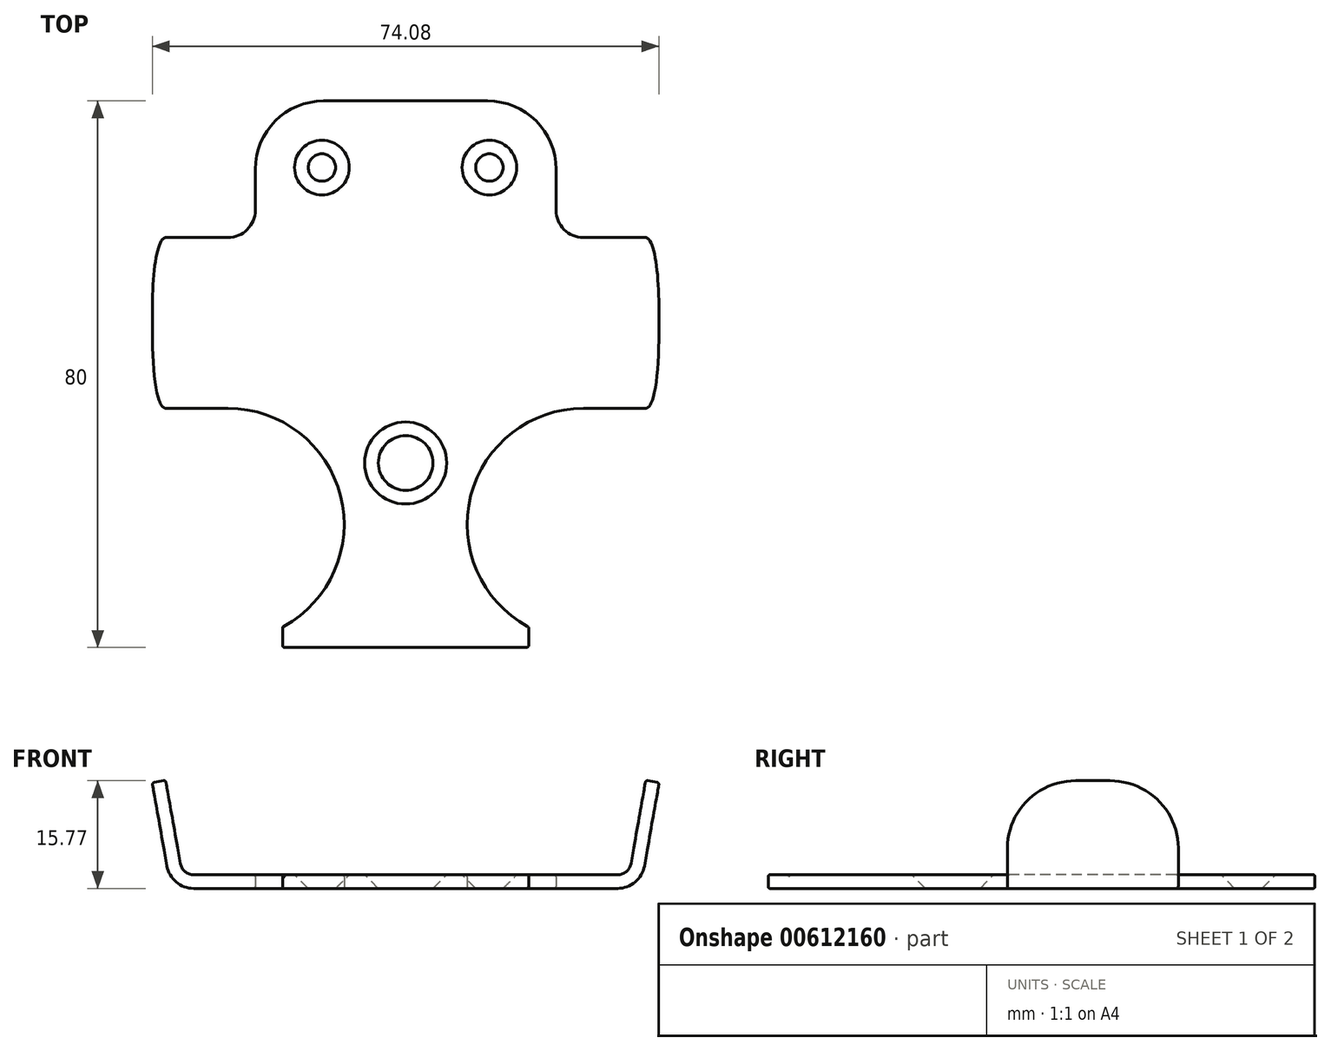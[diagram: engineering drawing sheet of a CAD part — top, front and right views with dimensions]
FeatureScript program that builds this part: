
annotation { "Feature Type Name" : "Feature", "Feature Type Description" : "" }
export const myFeature = defineFeature(function(context is Context, id is Id, definition is map)
    precondition{}
    {
        {
            var Q0;
            Q0=qCreatedBy(makeId("Top.planeOp"),FACE);
            var sketch = newSketch(context, id + "F0", { "sketchPlane" : qUnion([Q0])});
            skLineSegment(sketch, "E0", {"start": v(0, -42) * mm, "end": v(0, 38) * mm, "construction": true});
            skLineSegment(sketch, "E1", {"start": v(0, 38) * mm, "end": v(-12, 38) * mm});
            skArc(sketch, "E2", {"start": v(-12, 38) * mm, "mid": v(-19.07, 35.07) * mm, "end": v(-22, 28) * mm});
            skLineSegment(sketch, "E3", {"start": v(-22, 28) * mm, "end": v(-22, 22) * mm});
            skArc(sketch, "E4", {"start": v(-22, 22) * mm, "mid": v(-23.17, 19.17) * mm, "end": v(-26, 18) * mm});
            skLineSegment(sketch, "E5", {"start": v(-26, 18) * mm, "end": v(-28.5, 18) * mm});
            skLineSegment(sketch, "E6", {"start": v(-28.5, 18) * mm, "end": v(-28.5, -7) * mm});
            skLineSegment(sketch, "E7", {"start": v(-28.5, -7) * mm, "end": v(-26, -7) * mm});
            skArc(sketch, "E8", {"start": v(-18, -39) * mm, "mid": v(-9.5, -19.88) * mm, "end": v(-26, -7) * mm});
            skLineSegment(sketch, "E9", {"start": v(-18, -39) * mm, "end": v(-18, -42) * mm});
            skLineSegment(sketch, "E10", {"start": v(-18, -42) * mm, "end": v(0, -42) * mm});
            skLineSegment(sketch, "E11.MirrorCS", {"start": v(0, 38) * mm, "end": v(12, 38) * mm});
            skArc(sketch, "E12.MirrorCS", {"start": v(12, 38) * mm, "mid": v(19.07, 35.07) * mm, "end": v(22, 28) * mm});
            skLineSegment(sketch, "E13.MirrorCS", {"start": v(22, 28) * mm, "end": v(22, 22) * mm});
            skArc(sketch, "E14.MirrorCS", {"start": v(22, 22) * mm, "mid": v(23.17, 19.17) * mm, "end": v(26, 18) * mm});
            skLineSegment(sketch, "E15.MirrorCS", {"start": v(26, 18) * mm, "end": v(28.5, 18) * mm});
            skLineSegment(sketch, "E16.MirrorCS", {"start": v(28.5, 18) * mm, "end": v(28.5, -7) * mm});
            skLineSegment(sketch, "E17.MirrorCS", {"start": v(28.5, -7) * mm, "end": v(26, -7) * mm});
            skArc(sketch, "E18.MirrorCS", {"start": v(18, -39) * mm, "mid": v(9.5, -19.88) * mm, "end": v(26, -7) * mm});
            skLineSegment(sketch, "E19.MirrorCS", {"start": v(18, -39) * mm, "end": v(18, -42) * mm});
            skLineSegment(sketch, "E20.MirrorCS", {"start": v(18, -42) * mm, "end": v(0, -42) * mm});
            skSolve(sketch);
        }
        {
            var Q0;
            Q0 = qSketchRegion(id + "F0", true);
            extrude(context, id + "F1", {"entities" : qUnion([Q0]), "depth" : 2 * mm, "offsetDistance" : 25 * mm});
        }
        {
            var Q0;
            Q0=makeQuery(id+"F1.opExtrude","SWEPT_FACE",FACE,{"disambiguationData":[OSD([sQuery(id+"F0.wireOp",EDGE,"E7")])]});
            var sketch = newSketch(context, id + "F2", { "sketchPlane" : qUnion([Q0])});
            skLineSegment(sketch, "E21", {"start": v(-28.5, 0) * mm, "end": v(-31, 0) * mm});
            skArc(sketch, "E22", {"start": v(-34.94, 3.3) * mm, "mid": v(-33.57, 0.94) * mm, "end": v(-31, 0) * mm});
            skLineSegment(sketch, "E23", {"start": v(-34.94, 3.3) * mm, "end": v(-35.35, 5.62) * mm});
            skLineSegment(sketch, "E24", {"start": v(-35.35, 5.62) * mm, "end": v(-33.38, 5.97) * mm});
            skLineSegment(sketch, "E25", {"start": v(-33.38, 5.97) * mm, "end": v(-32.97, 3.65) * mm});
            skArc(sketch, "E26", {"start": v(-32.97, 3.65) * mm, "mid": v(-32.29, 2.47) * mm, "end": v(-31, 2) * mm});
            skLineSegment(sketch, "E27", {"start": v(-31, 2) * mm, "end": v(-28.5, 2) * mm});
            skSolve(sketch);
        }
        {
            var Q0;
            Q0 = qSketchRegion(id + "F2", true);
            var Q1;
            Q1=makeQuery(id+"F2.imprint","IMPRINT",FACE,{"disambiguationData":[TD([[makeQuery(id+"F2.imprint","IMPRINT",EDGE,{"derivedFrom":sQuery(id+"F2.wireOp",EDGE,"E21")}),-1.0]])]});
            var Q2;
            Q2=makeQuery(id+"F1.opExtrude","SWEPT_FACE",FACE,{"disambiguationData":[OSD([sQuery(id+"F0.wireOp",EDGE,"E5")])]});
            extrude(context, id + "F3", {"entities" : qUnion([Q0, Q1]), "endBound" : BoundingType.UP_TO_SURFACE, "oppositeDirection" : true, "depth" : 25 * mm, "endBoundEntityFace" : qUnion([Q2]), "offsetDistance" : 25 * mm});
        }
        {
            var Q0;
            Q0=makeQuery(id+"F3.opExtrude","SWEPT_FACE",FACE,{"disambiguationData":[OSD([sQuery(id+"F2.wireOp",EDGE,"E23")])]});
            var sketch = newSketch(context, id + "F4", { "sketchPlane" : qUnion([Q0])});
            skArc(sketch, "E28", {"start": v(-8, 21.67) * mm, "mid": v(-15.07, 18.75) * mm, "end": v(-18, 11.67) * mm});
            skArc(sketch, "E29", {"start": v(7, 11.67) * mm, "mid": v(4.07, 18.75) * mm, "end": v(-3, 21.67) * mm});
            skLineSegment(sketch, "E30", {"start": v(-3, 21.67) * mm, "end": v(-8, 21.67) * mm});
            skSolve(sketch);
        }
        {
            var Q0;
            Q0 = qSketchRegion(id + "F4", true);
            var Q1;
            Q1=makeQuery(id+"F4.imprint","IMPRINT",FACE,{"disambiguationData":[TD([[makeQuery(id+"F4.imprint","IMPRINT",EDGE,{"derivedFrom":sQuery(id+"F4.wireOp",EDGE,"E28")}),1.0]])]});
            var Q2;
            Q2=makeQuery(id+"F3.opExtrude","SWEPT_FACE",FACE,{"disambiguationData":[OSD([sQuery(id+"F2.wireOp",EDGE,"E25")])]});
            extrude(context, id + "F5", {"entities" : qUnion([Q0, Q1]), "operationType" : NewBodyOperationType.ADD, "endBound" : BoundingType.UP_TO_SURFACE, "oppositeDirection" : true, "depth" : 25 * mm, "endBoundEntityFace" : qUnion([Q2]), "offsetDistance" : 25 * mm});
        }
        {
            var Q0;
            Q0=makeQuery(id+"F3.opExtrude","SWEPT_BODY",BODY,{"disambiguationData":[OSD([sQuery(id+"F0.wireOp",EDGE,"E6"),sQuery(id+"F0.wireOp",EDGE,"E7"),sQuery(id+"F2.wireOp",EDGE,"E21"),sQuery(id+"F2.wireOp",EDGE,"E22"),sQuery(id+"F2.wireOp",EDGE,"E23"),sQuery(id+"F2.wireOp",EDGE,"E24"),sQuery(id+"F2.wireOp",EDGE,"E25"),sQuery(id+"F2.wireOp",EDGE,"E26"),sQuery(id+"F2.wireOp",EDGE,"E27")])]});
            var Q1;
            Q1=qCreatedBy(makeId("Right.planeOp"),FACE);
            mirror(context, id + "F6", {"operationType" : NewBodyOperationType.ADD, "entities" : qUnion([Q0]), "mirrorPlane" : qUnion([Q1])});
        }
        {
            var Q0;
            {var subQ0=makeQuery(id+"F3.opExtrude","SWEPT_FACE",FACE,{"disambiguationData":[OSD([sQuery(id+"F2.wireOp",EDGE,"E27")])]});Q0=makeQuery(id+"F6.boolean.opBoolean","MERGE",FACE,{"derivedFrom":[makeQuery(id+"F1.opExtrude","CAP_FACE",FACE,{"disambiguationData":[OSD([sQuery(id+"F0.wireOp",EDGE,"E1"),sQuery(id+"F0.wireOp",EDGE,"E2"),sQuery(id+"F0.wireOp",EDGE,"E3"),sQuery(id+"F0.wireOp",EDGE,"E4"),sQuery(id+"F0.wireOp",EDGE,"E5"),sQuery(id+"F0.wireOp",EDGE,"E6"),sQuery(id+"F0.wireOp",EDGE,"E7"),sQuery(id+"F0.wireOp",EDGE,"E8"),sQuery(id+"F0.wireOp",EDGE,"E9"),sQuery(id+"F0.wireOp",EDGE,"E10"),sQuery(id+"F0.wireOp",EDGE,"E11.MirrorCS"),sQuery(id+"F0.wireOp",EDGE,"E12.MirrorCS"),sQuery(id+"F0.wireOp",EDGE,"E13.MirrorCS"),sQuery(id+"F0.wireOp",EDGE,"E14.MirrorCS"),sQuery(id+"F0.wireOp",EDGE,"E15.MirrorCS"),sQuery(id+"F0.wireOp",EDGE,"E16.MirrorCS"),sQuery(id+"F0.wireOp",EDGE,"E17.MirrorCS"),sQuery(id+"F0.wireOp",EDGE,"E18.MirrorCS"),sQuery(id+"F0.wireOp",EDGE,"E19.MirrorCS"),sQuery(id+"F0.wireOp",EDGE,"E20.MirrorCS")])],"isStart":false}),subQ0,makeQuery(id+"F6.opPattern","COPY",FACE,{"derivedFrom":subQ0,"instanceName":"1"})]});}
            var sketch = newSketch(context, id + "F7", { "sketchPlane" : qUnion([Q0])});
            skCircle(sketch, "E31", {"center": v(-12.25, 28.25) * mm, "radius": 2 * mm});
            skCircle(sketch, "E32", {"center": v(12.25, 28.25) * mm, "radius": 2 * mm});
            skCircle(sketch, "E33", {"center": v(0, -15) * mm, "radius": 4 * mm});
            skSolve(sketch);
        }
        {
            var Q0;
            Q0=sQuery(id+"F7.wireOp",VERTEX,"E32.center");
            var Q1;
            Q1=sQuery(id+"F7.wireOp",VERTEX,"E31.center");
            var Q2;
            Q2=makeQuery(id+"F1.opExtrude","SWEPT_BODY",BODY,{"disambiguationData":[OSD([sQuery(id+"F0.wireOp",EDGE,"E1"),sQuery(id+"F0.wireOp",EDGE,"E2"),sQuery(id+"F0.wireOp",EDGE,"E3"),sQuery(id+"F0.wireOp",EDGE,"E4"),sQuery(id+"F0.wireOp",EDGE,"E5"),sQuery(id+"F0.wireOp",EDGE,"E6"),sQuery(id+"F0.wireOp",EDGE,"E7"),sQuery(id+"F0.wireOp",EDGE,"E8"),sQuery(id+"F0.wireOp",EDGE,"E9"),sQuery(id+"F0.wireOp",EDGE,"E10"),sQuery(id+"F0.wireOp",EDGE,"E11.MirrorCS"),sQuery(id+"F0.wireOp",EDGE,"E12.MirrorCS"),sQuery(id+"F0.wireOp",EDGE,"E13.MirrorCS"),sQuery(id+"F0.wireOp",EDGE,"E14.MirrorCS"),sQuery(id+"F0.wireOp",EDGE,"E15.MirrorCS"),sQuery(id+"F0.wireOp",EDGE,"E16.MirrorCS"),sQuery(id+"F0.wireOp",EDGE,"E17.MirrorCS"),sQuery(id+"F0.wireOp",EDGE,"E18.MirrorCS"),sQuery(id+"F0.wireOp",EDGE,"E19.MirrorCS"),sQuery(id+"F0.wireOp",EDGE,"E20.MirrorCS")])]});
            hole(context, id + "F8", {"style" : HoleStyle.C_SINK, "endStyle" : HoleEndStyle.THROUGH, "holeDiameter" : 4 * mm, "cSinkDiameter" : 8 * mm, "cSinkAngle" : 90 * degree, "majorDiameter" : 5 * mm, "isTappedThrough" : true, "tappedDepth" : 12 * mm, "tapClearance" : 3, "locations" : qUnion([Q0, Q1]), "scope" : qUnion([Q2])});
        }
        {
            var Q0;
            Q0=sQuery(id+"F7.wireOp",VERTEX,"E33.center");
            var Q1;
            Q1=makeQuery(id+"F1.opExtrude","SWEPT_BODY",BODY,{"disambiguationData":[OSD([sQuery(id+"F0.wireOp",EDGE,"E1"),sQuery(id+"F0.wireOp",EDGE,"E2"),sQuery(id+"F0.wireOp",EDGE,"E3"),sQuery(id+"F0.wireOp",EDGE,"E4"),sQuery(id+"F0.wireOp",EDGE,"E5"),sQuery(id+"F0.wireOp",EDGE,"E6"),sQuery(id+"F0.wireOp",EDGE,"E7"),sQuery(id+"F0.wireOp",EDGE,"E8"),sQuery(id+"F0.wireOp",EDGE,"E9"),sQuery(id+"F0.wireOp",EDGE,"E10"),sQuery(id+"F0.wireOp",EDGE,"E11.MirrorCS"),sQuery(id+"F0.wireOp",EDGE,"E12.MirrorCS"),sQuery(id+"F0.wireOp",EDGE,"E13.MirrorCS"),sQuery(id+"F0.wireOp",EDGE,"E14.MirrorCS"),sQuery(id+"F0.wireOp",EDGE,"E15.MirrorCS"),sQuery(id+"F0.wireOp",EDGE,"E16.MirrorCS"),sQuery(id+"F0.wireOp",EDGE,"E17.MirrorCS"),sQuery(id+"F0.wireOp",EDGE,"E18.MirrorCS"),sQuery(id+"F0.wireOp",EDGE,"E19.MirrorCS"),sQuery(id+"F0.wireOp",EDGE,"E20.MirrorCS")])]});
            hole(context, id + "F9", {"style" : HoleStyle.C_SINK, "endStyle" : HoleEndStyle.THROUGH, "holeDiameter" : 8 * mm, "cSinkDiameter" : 12 * mm, "cSinkAngle" : 90 * degree, "majorDiameter" : 5 * mm, "isTappedThrough" : true, "tappedDepth" : 12 * mm, "tapClearance" : 3, "locations" : qUnion([Q0]), "scope" : qUnion([Q1])});
        }
        {
            var Q0;
            Q0=makeQuery(id+"F1.opExtrude","CAP_EDGE",EDGE,{"disambiguationData":[OSD([sQuery(id+"F0.wireOp",EDGE,"E18.MirrorCS")])],"isStart":false});
            var Q1;
            Q1=makeQuery(id+"F1.opExtrude","CAP_EDGE",EDGE,{"disambiguationData":[OSD([sQuery(id+"F0.wireOp",EDGE,"E19.MirrorCS")])],"isStart":false});
            var Q2;
            Q2=makeQuery(id+"F1.opExtrude","CAP_EDGE",EDGE,{"disambiguationData":[OSD([sQuery(id+"F0.wireOp",EDGE,"E10"),sQuery(id+"F0.wireOp",EDGE,"E20.MirrorCS")])],"isStart":false});
            var Q3;
            Q3=makeQuery(id+"F1.opExtrude","SWEPT_EDGE",EDGE,{"disambiguationData":[OSD([sQuery(id+"F0.wireOp",EDGE,"E19.MirrorCS"),sQuery(id+"F0.wireOp",EDGE,"E20.MirrorCS")])]});
            var Q4;
            Q4=makeQuery(id+"F1.opExtrude","CAP_EDGE",EDGE,{"disambiguationData":[OSD([sQuery(id+"F0.wireOp",EDGE,"E19.MirrorCS")])],"isStart":true});
            var Q5;
            Q5=makeQuery(id+"F1.opExtrude","CAP_EDGE",EDGE,{"disambiguationData":[OSD([sQuery(id+"F0.wireOp",EDGE,"E18.MirrorCS")])],"isStart":true});
            var Q6;
            Q6=makeQuery(id+"F1.opExtrude","CAP_EDGE",EDGE,{"disambiguationData":[OSD([sQuery(id+"F0.wireOp",EDGE,"E10"),sQuery(id+"F0.wireOp",EDGE,"E20.MirrorCS")])],"isStart":true});
            var Q7;
            Q7=makeQuery(id+"F1.opExtrude","CAP_EDGE",EDGE,{"disambiguationData":[OSD([sQuery(id+"F0.wireOp",EDGE,"E9")])],"isStart":true});
            var Q8;
            Q8=makeQuery(id+"F1.opExtrude","SWEPT_EDGE",EDGE,{"disambiguationData":[OSD([sQuery(id+"F0.wireOp",EDGE,"E8"),sQuery(id+"F0.wireOp",EDGE,"E9")])]});
            var Q9;
            Q9=makeQuery(id+"F1.opExtrude","SWEPT_EDGE",EDGE,{"disambiguationData":[OSD([sQuery(id+"F0.wireOp",EDGE,"E9"),sQuery(id+"F0.wireOp",EDGE,"E10")])]});
            var Q10;
            Q10=makeQuery(id+"F1.opExtrude","SWEPT_EDGE",EDGE,{"disambiguationData":[OSD([sQuery(id+"F0.wireOp",EDGE,"E18.MirrorCS"),sQuery(id+"F0.wireOp",EDGE,"E19.MirrorCS")])]});
            fillet(context, id + "F10", {"entities" : qUnion([Q0, Q1, Q2, Q3, Q4, Q5, Q6, Q7, Q8, Q9, Q10]), "radius" : 0.3 * mm, "tangentPropagation" : true, "allowEdgeOverflow" : false});
        }
    });
